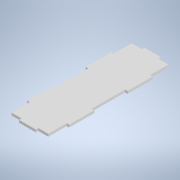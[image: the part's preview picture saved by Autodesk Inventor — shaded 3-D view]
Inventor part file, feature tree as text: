
AUTODESK INVENTOR PART (.ipt)
format: ipt  version: 2020.3 (Build 243373000, 373)  size: 152,064 bytes
history: native  units: mm
features: extrude x2, sketch x2
ambient origin geometry x8: Origin, YZ Plane, XZ Plane, XY Plane, X Axis, Y Axis, Z Axis, Center Point
bodies: Solid1 (feature_tree)
feature tree (4):
  extrude  "Base"  Depth=50.0mm
  extrude  "Tabs"  Depth=25.0mm
  sketch  "Sketch1"  dims[d0=150.0mm d1=50.0mm]
  sketch  "Sketch2"  dims[d2=3.0mm d3=0.0mm d10=25.0mm d11=25.0mm d12=30.0mm d13=30.0mm d14=40.0mm d15=3.0mm d16=0.0mm d17=0.0mm d21=3.0mm d22=10.0mm]
